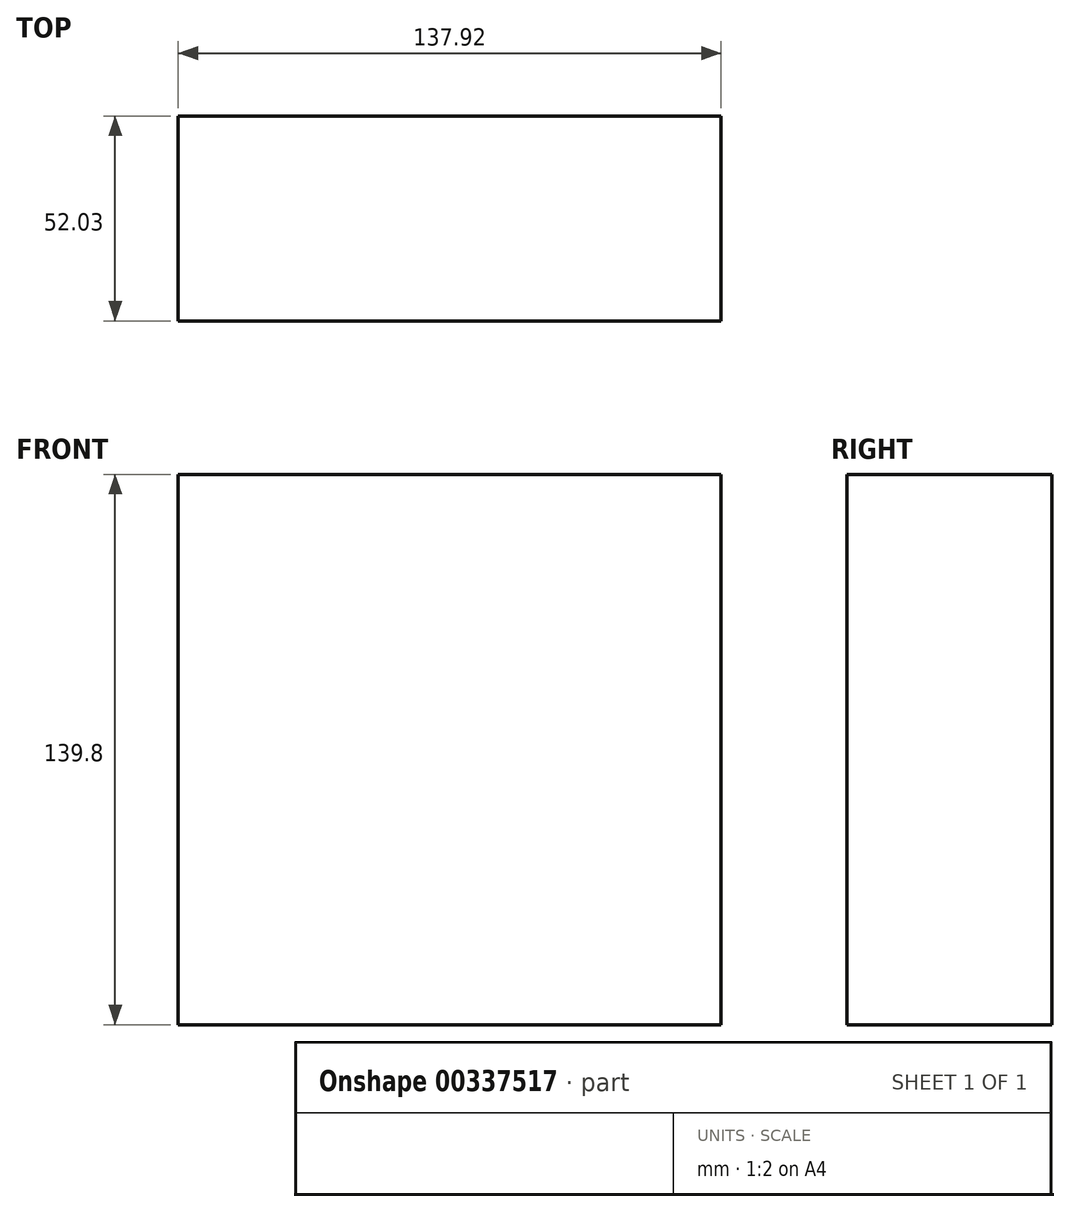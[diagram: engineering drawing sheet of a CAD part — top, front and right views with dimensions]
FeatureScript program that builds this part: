
annotation { "Feature Type Name" : "Feature", "Feature Type Description" : "" }
export const myFeature = defineFeature(function(context is Context, id is Id, definition is map)
    precondition{}
    {
        {
            var Q0;
            Q0=qCreatedBy(makeId("Front.planeOp"),FACE);
            var sketch = newSketch(context, id + "F0", { "sketchPlane" : qUnion([Q0])});
            skLineSegment(sketch, "E0.bottom", {"start": v(68.96, 69.9) * mm, "end": v(-68.96, 69.9) * mm});
            skLineSegment(sketch, "E0.top", {"start": v(68.96, -69.9) * mm, "end": v(-68.96, -69.9) * mm});
            skLineSegment(sketch, "E0.left", {"start": v(68.96, 69.9) * mm, "end": v(68.96, -69.9) * mm});
            skLineSegment(sketch, "E0.right", {"start": v(-68.96, 69.9) * mm, "end": v(-68.96, -69.9) * mm});
            skPoint(sketch, "E0.middle", {"position": v(0, 0) * mm});
            skSolve(sketch);
        }
        {
            var Q0;
            Q0=makeQuery(id+"F0.imprint","IMPRINT",FACE,{"disambiguationData":[TD([[makeQuery(id+"F0.imprint","IMPRINT",EDGE,{"derivedFrom":sQuery(id+"F0.wireOp",EDGE,"E0.bottom")}),1.0]])]});
            extrude(context, id + "F1", {"entities" : qUnion([Q0]), "depth" : 52.03 * mm});
        }
    });
